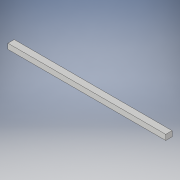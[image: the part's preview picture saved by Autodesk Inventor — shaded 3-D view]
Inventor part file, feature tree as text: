
AUTODESK INVENTOR PART (.ipt)
format: ipt  version: 2019 (Build 230136000, 136)  size: 92,672 bytes
history: native  units: mm
features: extrude x1, sketch x1
ambient origin geometry x8: Origin, YZ Plane, XZ Plane, XY Plane, X Axis, Y Axis, Z Axis, Center Point
bodies: Solid1 (feature_tree)
feature tree (2):
  extrude  "Extrusion1"  Depth=5.0mm
  sketch  "Sketch1"  dims[d0=148.627mm d1=5.0mm d2=6.0mm d3=0.0mm]
